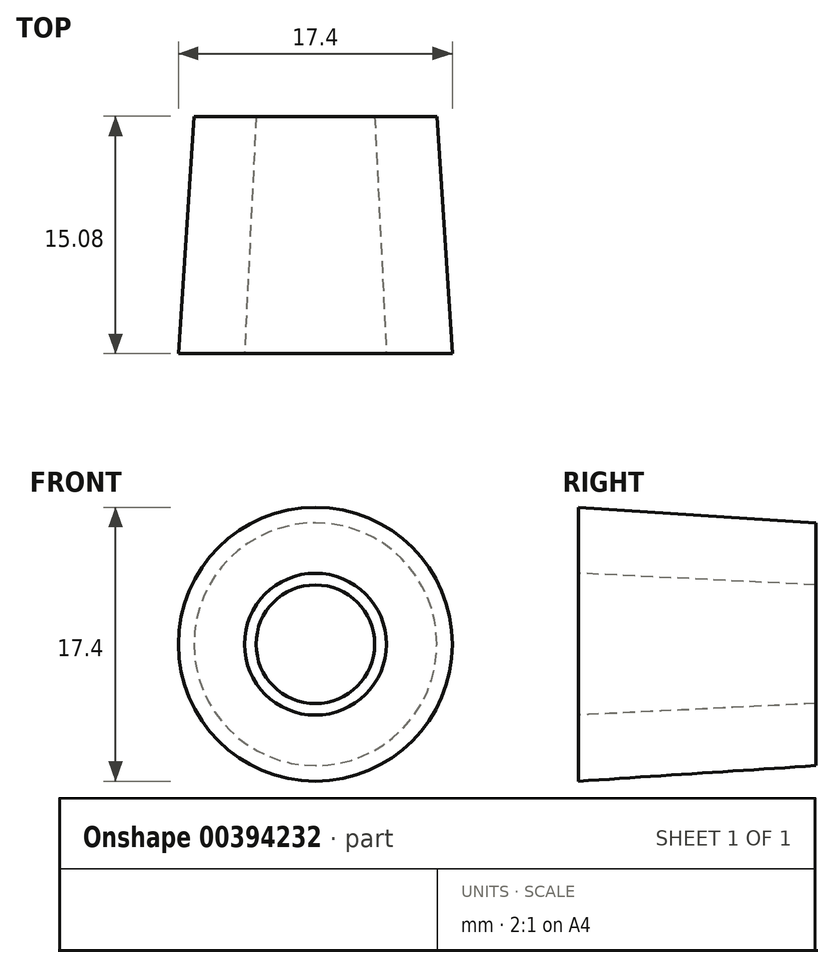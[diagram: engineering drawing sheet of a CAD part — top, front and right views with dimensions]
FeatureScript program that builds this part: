
annotation { "Feature Type Name" : "Feature", "Feature Type Description" : "" }
export const myFeature = defineFeature(function(context is Context, id is Id, definition is map)
    precondition{}
    {
        {
            var Q0;
            Q0=qCreatedBy(makeId("Top.planeOp"),FACE);
            var sketch = newSketch(context, id + "F0", { "sketchPlane" : qUnion([Q0])});
            skLineSegment(sketch, "E0", {"start": v(8.7, 0) * mm, "end": v(7.71, 15.08) * mm});
            skLineSegment(sketch, "E1", {"start": v(4.5, 0) * mm, "end": v(3.77, 15.08) * mm});
            skLineSegment(sketch, "E2", {"start": v(3.77, 15.08) * mm, "end": v(7.71, 15.08) * mm});
            skLineSegment(sketch, "E3", {"start": v(3.77, 15.08) * mm, "end": v(4.5, 0) * mm});
            skLineSegment(sketch, "E4", {"start": v(8.7, 0) * mm, "end": v(4.5, 0) * mm});
            skLineSegment(sketch, "E5", {"start": v(0, 0) * mm, "end": v(0, 16.54) * mm});
            skSolve(sketch);
        }
        {
            var Q0;
            Q0=makeQuery(id+"F0.imprint","IMPRINT",FACE,{"disambiguationData":[TD([[makeQuery(id+"F0.imprint","IMPRINT",EDGE,{"derivedFrom":sQuery(id+"F0.wireOp",EDGE,"E2")}),-1.0]])]});
            var Q1;
            Q1=sQuery(id+"F0.wireOp",EDGE,"E5");
            revolve(context, id + "F1", {"entities" : qUnion([Q0]), "axis" : qUnion([Q1]), "revolveType" : RevolveType.FULL});
        }
    });
